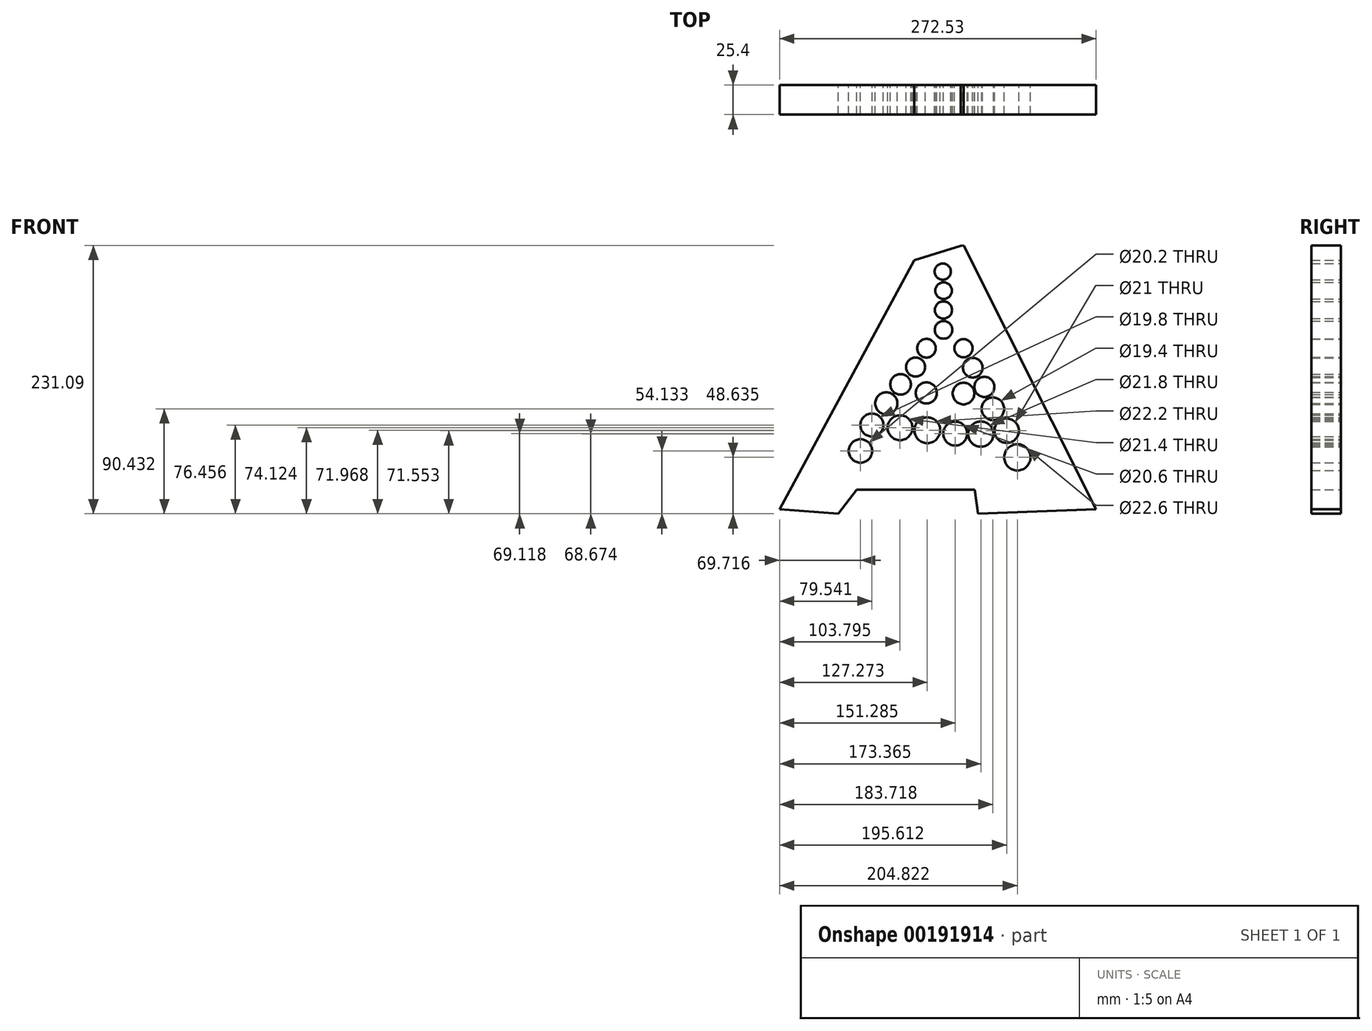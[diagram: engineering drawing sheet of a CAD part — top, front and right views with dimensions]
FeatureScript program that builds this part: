
annotation { "Feature Type Name" : "Feature", "Feature Type Description" : "" }
export const myFeature = defineFeature(function(context is Context, id is Id, definition is map)
    precondition{}
    {
        {
            var Q0;
            Q0=qCreatedBy(makeId("Front.planeOp"),FACE);
            var sketch = newSketch(context, id + "F0", { "sketchPlane" : qUnion([Q0])});
            skCircle(sketch, "E0", {"center": v(-17.84, 134.12) * mm, "radius": 7 * mm});
            skCircle(sketch, "E1", {"center": v(-17.14, 117.72) * mm, "radius": 7.2 * mm});
            skCircle(sketch, "E2", {"center": v(-17.25, 101.1) * mm, "radius": 7.4 * mm});
            skCircle(sketch, "E3", {"center": v(-17.18, 84.01) * mm, "radius": 7.6 * mm});
            skCircle(sketch, "E4", {"center": v(-31.86, 68.18) * mm, "radius": 8 * mm});
            skCircle(sketch, "E5", {"center": v(0, 68.18) * mm, "radius": 7.8 * mm});
            skCircle(sketch, "E6", {"center": v(-41.23, 51.97) * mm, "radius": 8.22 * mm});
            skCircle(sketch, "E7", {"center": v(8, 51.43) * mm, "radius": 8.45 * mm});
            skCircle(sketch, "E8", {"center": v(-54.18, 37.1) * mm, "radius": 8.85 * mm});
            skCircle(sketch, "E9", {"center": v(18, 34.88) * mm, "radius": 8.65 * mm});
            skCircle(sketch, "E10", {"center": v(-31.99, 29.7) * mm, "radius": 9.1 * mm});
            skCircle(sketch, "E11", {"center": v(0, 29.18) * mm, "radius": 9.3 * mm});
            skCircle(sketch, "E12", {"center": v(-66.46, 20.73) * mm, "radius": 9.5 * mm});
            skCircle(sketch, "E13", {"center": v(25.29, 16.07) * mm, "radius": 9.7 * mm});
            skCircle(sketch, "E14", {"center": v(-78.89, 2.1) * mm, "radius": 9.9 * mm});
            skCircle(sketch, "E15", {"center": v(37.18, -2.8) * mm, "radius": 10.5 * mm});
            skCircle(sketch, "E16", {"center": v(-88.71, -20.23) * mm, "radius": 10.1 * mm});
            skCircle(sketch, "E17", {"center": v(-7.14, -5.24) * mm, "radius": 10.3 * mm});
            skCircle(sketch, "E18", {"center": v(-54.63, -0.24) * mm, "radius": 10.7 * mm});
            skCircle(sketch, "E19", {"center": v(-31.16, -2.4) * mm, "radius": 11.1 * mm});
            skCircle(sketch, "E20", {"center": v(14.94, -5.69) * mm, "radius": 10.9 * mm});
            skCircle(sketch, "E21", {"center": v(46.4, -25.73) * mm, "radius": 11.3 * mm});
            skSolve(sketch);
        }
        {
            var Q0;
            Q0=qCreatedBy(makeId("Front.planeOp"),FACE);
            var sketch = newSketch(context, id + "F1", { "sketchPlane" : qUnion([Q0])});
            skLineSegment(sketch, "E22", {"start": v(-42.3, 144) * mm, "end": v(-158.43, -70.24) * mm});
            skLineSegment(sketch, "E23", {"start": v(-158.43, -70.24) * mm, "end": v(-107.8, -74.36) * mm});
            skLineSegment(sketch, "E24", {"start": v(-107.8, -74.36) * mm, "end": v(-91.89, -53.67) * mm});
            skLineSegment(sketch, "E25", {"start": v(-91.89, -53.67) * mm, "end": v(9.71, -53.67) * mm});
            skLineSegment(sketch, "E26", {"start": v(9.71, -53.67) * mm, "end": v(12.58, -74.36) * mm});
            skLineSegment(sketch, "E27", {"start": v(12.58, -74.36) * mm, "end": v(114.1, -70.24) * mm});
            skLineSegment(sketch, "E28", {"start": v(114.1, -70.24) * mm, "end": v(0.08, 156.73) * mm});
            skLineSegment(sketch, "E29", {"start": v(-42.3, 144) * mm, "end": v(-2.39, 156.21) * mm});
            skLineSegment(sketch, "E30", {"start": v(0.08, 156.73) * mm, "end": v(-2.39, 156.21) * mm});
            skSolve(sketch);
        }
        {
            var Q0;
            Q0 = qSketchRegion(id + "F1", true);
            extrude(context, id + "F2", {"entities" : qUnion([Q0]), "depth" : 25.4 * mm});
        }
        {
            var Q0;
            Q0 = qSketchRegion(id + "F0", true);
            extrude(context, id + "F3", {"entities" : qUnion([Q0]), "operationType" : NewBodyOperationType.REMOVE, "endBound" : BoundingType.THROUGH_ALL, "depth" : 25.4 * mm});
        }
    });
